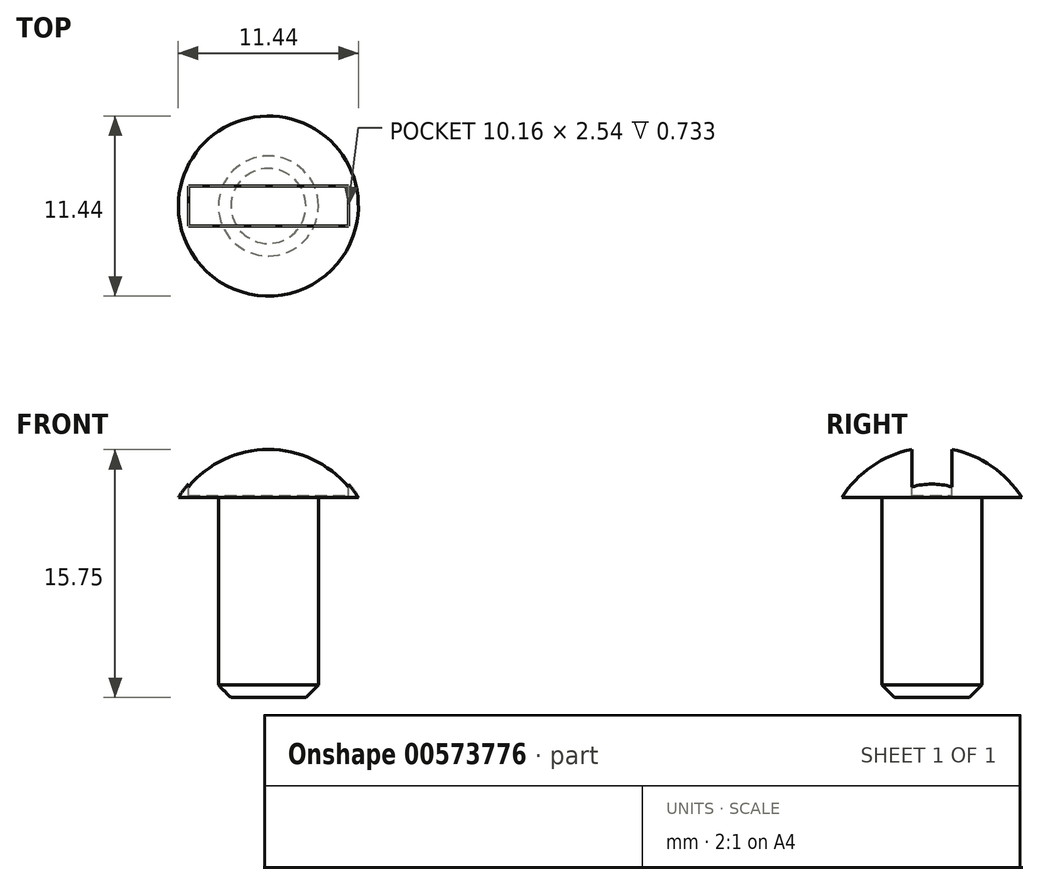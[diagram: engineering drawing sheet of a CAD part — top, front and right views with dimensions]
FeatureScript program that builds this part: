
annotation { "Feature Type Name" : "Feature", "Feature Type Description" : "" }
export const myFeature = defineFeature(function(context is Context, id is Id, definition is map)
    precondition{}
    {
        {
            var Q0;
            Q0=qCreatedBy(makeId("Front.planeOp"),FACE);
            var sketch = newSketch(context, id + "F0", { "sketchPlane" : qUnion([Q0])});
            skLineSegment(sketch, "E0", {"start": v(0, 0) * mm, "end": v(0, 15.88) * mm});
            skLineSegment(sketch, "E1", {"start": v(0, 0) * mm, "end": v(3.17, 0) * mm});
            skLineSegment(sketch, "E2", {"start": v(3.17, 0) * mm, "end": v(3.17, 12.7) * mm});
            skLineSegment(sketch, "E3", {"start": v(3.17, 12.7) * mm, "end": v(5.72, 12.7) * mm});
            skArc(sketch, "E4", {"start": v(5.72, 12.7) * mm, "mid": v(3.27, 15.03) * mm, "end": v(0, 15.88) * mm});
            skSolve(sketch);
        }
        {
            var Q0;
            Q0=makeQuery(id+"F0.imprint","IMPRINT",FACE,{"disambiguationData":[TD([[makeQuery(id+"F0.imprint","IMPRINT",EDGE,{"derivedFrom":sQuery(id+"F0.wireOp",EDGE,"E0")}),-1.0]])]});
            var Q1;
            Q1=sQuery(id+"F0.wireOp",EDGE,"E0");
            revolve(context, id + "F1", {"entities" : qUnion([Q0]), "axis" : qUnion([Q1]), "revolveType" : RevolveType.FULL});
        }
        {
            var Q0;
            Q0=qCreatedBy(makeId("Top.planeOp"),FACE);
            cPlane(context, id + "F2", {"entities" : qUnion([Q0]), "cplaneType" : CPlaneType.OFFSET, "offset" : 15.88 * mm, "width" : 152.4 * mm, "height" : 152.4 * mm});
        }
        {
            var Q0;
            Q0=qCreatedBy(id+"F2.planeOp",FACE);
            var sketch = newSketch(context, id + "F3", { "sketchPlane" : qUnion([Q0])});
            skLineSegment(sketch, "E5.bottom", {"start": v(-5.08, -1.27) * mm, "end": v(5.08, -1.27) * mm});
            skLineSegment(sketch, "E5.top", {"start": v(-5.08, 1.27) * mm, "end": v(5.08, 1.27) * mm});
            skLineSegment(sketch, "E5.left", {"start": v(-5.08, -1.27) * mm, "end": v(-5.08, 1.27) * mm});
            skLineSegment(sketch, "E5.right", {"start": v(5.08, -1.27) * mm, "end": v(5.08, 1.27) * mm});
            skPoint(sketch, "E5.middle", {"position": v(0, 0) * mm});
            skSolve(sketch);
        }
        {
            var Q0;
            Q0 = qSketchRegion(id + "F3", true);
            extrude(context, id + "F4", {"entities" : qUnion([Q0]), "operationType" : NewBodyOperationType.REMOVE, "oppositeDirection" : true, "depth" : 3.05 * mm, "offsetDistance" : 25.4 * mm});
        }
        {
            var Q0;
            Q0=makeQuery(id+"F1.opRevolve","SWEPT_EDGE",EDGE,{"disambiguationData":[OSD([sQuery(id+"F0.wireOp",EDGE,"E1"),sQuery(id+"F0.wireOp",EDGE,"E2")])]});
            chamfer(context, id + "F5", {"entities" : qUnion([Q0]), "width" : 0.8 * mm, "tangentPropagation" : true});
        }
    });
